FCSTD DOCUMENT  (FreeCAD 0.21R33771 (Git))
Label: grid
License: All rights reserved
LicenseURL: http://en.wikipedia.org/wiki/All_rights_reserved
objects: Sketcher::SketchObject×1, PartDesign::Body×1
note: 2 computed .brp shape members not serialized (recipe doc carries the construction recipe); baked Part::Feature solids carry a one-line shape summary decoded from their .brp

FEATURE [Sketcher::SketchObject] Sketch
  FullyConstrained = false
  MapMode = 5
  Support = -> [XY_Plane]
  sketch-geometry (12):
    g0: LineSegment StartX=-223.52 StartY=-57.15 StartZ=0 EndX=-223.52 EndY=57.15 EndZ=0
    g1: LineSegment StartX=-223.52 StartY=57.15 StartZ=0 EndX=223.52 EndY=57.15 EndZ=0
    g2: LineSegment StartX=223.52 StartY=57.15 StartZ=0 EndX=223.52 EndY=-57.15 EndZ=0
    g3: LineSegment StartX=223.52 StartY=-57.15 StartZ=0 EndX=-223.52 EndY=-57.15 EndZ=0
    g4: GeomPoint X=0 Y=0 Z=0
    g5: LineSegment StartX=-223.52 StartY=57.15 StartZ=0 EndX=-213.995 EndY=57.15 EndZ=0
    g6: LineSegment StartX=-223.52 StartY=47.625 StartZ=0 EndX=-223.52 EndY=57.15 EndZ=0
    g7: LineSegment StartX=-220.98 StartY=54.61 StartZ=0 EndX=-220.98 EndY=40.64 EndZ=0
    g8: LineSegment StartX=-220.98 StartY=40.64 StartZ=0 EndX=-207.01 EndY=40.64 EndZ=0
    g9: LineSegment StartX=-207.01 StartY=40.64 StartZ=0 EndX=-207.01 EndY=54.61 EndZ=0
    g10: LineSegment StartX=-207.01 StartY=54.61 StartZ=0 EndX=-220.98 EndY=54.61 EndZ=0
    g11: GeomPoint X=-213.995 Y=47.625 Z=0
  constraints (41):
    c: Coincident(g0,g1)
    c: Coincident(g1,g2)
    c: Coincident(g2,g3)
    c: Coincident(g3,g0)
    c: Horizontal(g1)
    c: Horizontal(g3)
    c: Vertical(g0)
    c: Vertical(g2)
    c: Symmetric(g1,g0,g4)
    c: Coincident(g4,g-1)
    c: Coincident(g6,g5)
    c: Horizontal(g5)
    c: Vertical(g6)
    c: Coincident(g5,g0)
    c: Coincident(g7,g8)
    c: Coincident(g8,g9)
    c: Coincident(g9,g10)
    c: Coincident(g10,g7)
    c: Horizontal(g8)
    c: Horizontal(g10)
    c: Vertical(g7)
    c: Vertical(g9)
    c: Symmetric(g8,g7,g11)
    c: DistanceX(g9) = -207.01
    c: DistanceY(g9) = 54.61
    c: DistanceX(g7) = -220.98
    c: DistanceY(g7) = 54.61
    c: DistanceX(g8) = -207.01
    c: DistanceY(g8) = 40.64
    c: DistanceX(g7) = -220.98
    c: DistanceY(g7) = 40.64
    c: DistanceX(g0) = -223.52
    c: DistanceY(g0) = 57.15
    c: DistanceX(g4) = 0
    c: DistanceY(g4) = 0
    c: DistanceX(g0) = -223.52
    c: DistanceY(g0) = -57.15
    c: DistanceX(g2) = 223.52
    c: DistanceY(g2) = -57.15
    c: DistanceX(g1) = 223.52
    c: DistanceY(g1) = 57.15
FEATURE [PartDesign::Body] Body
  Group = -> [Sketch]
  Origin = -> Origin
